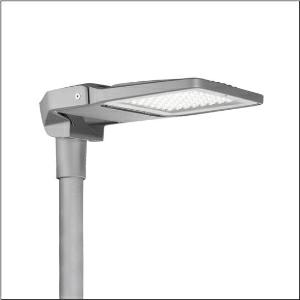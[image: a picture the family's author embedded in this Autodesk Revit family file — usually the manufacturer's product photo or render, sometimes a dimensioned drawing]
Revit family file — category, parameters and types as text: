
# Revit family: floodlight_fl_20_mini___pl61_5xa7672c1c4ac_7b6a
name_source: partatom
category: Lighting Fixtures
units: mm (PartAtom-declared; Revit-internal decimal feet)

## family parameters
Cut with Voids When Loaded = No
Host = Face
Light Source = No
Part Type = Normal
Room Calculation Point = No
Round Connector Dimension = Use Diameter
Shared = No

## types (1)
- --- (1 x LED 3000K / CRI = 80 (unbekannt), 9760 lm, 3000K)
    Apparent Load = 96 VA
    CIE Flux Codes = 33 65 98 100 100
    Color Rendering = 80
    Color Temperature = 3000K
    Default Elevation = 1800 mm
    Description = Floodlight FL 20 mini, floodlight, primary light control with lens, of plastic, primary optical cover: protective disc, of toughened safety glass, transparent, light distribution: PL61, light emission: direct distribution, primary light characteristic: asymmetric, installation type: side-entry, post-top, LED, High Power LED, rated luminous flux: 9.760lm, luminous efficacy: 102lm/W, light colour: 830, colour temperature: 3000K, control gear: ECG Plus, control: flexible luminous flux parameterisation, time-dependent luminous flux control, digital communication interface, overheat protection, power reduction, electronic power reduction, with terminal, 5-pole, max. 2.5mm², mains connection: 220..240V, AC, 50/60Hz, rated input power: 96W, LED unit, of diecast aluminium, powder-coated, Siteco® metallic grey (DB 702S), corrosivity category C5 mid according to DIN EN ISO 12944, incl. 1x M20 cable gland for cable Ø 6.5..12mm, inclination adjustable: 0°, 5°, 10°, 15°, please order mast flange separately, length: 565mm, width: 335mm, height: 119mm, housing frame, of diecast aluminium, powder-coated, Siteco® metallic grey (DB 702S), mast flange adapter, of diecast aluminium, powder-coated, Siteco® metallic grey (DB 702S), DALI, protection rating (complete): IP66, insulation class (complete): insulation class II (safety insulation), certification: CE, ENEC, VDE, protection symbol: D, permissible operating ambient temperature: -40..+40°C, permissible operating ambient temperature for outdoor applications: -40..+50°C, standard: DIN EN 12944, packaging unit: 1 piece

Light Distribution: PL61
    Height = 62 mm  [stored 0.203412 ft]
    Lamp = 1 x LED 3000K / CRI >= 80 (unbekannt)
    Lamp Light Flux = 9760 lm
    Lamp count = 1
    Length = 565 mm
    Luminous efficacy = 102 lm/W
    Manufacturer = Siteco
    ModVariant = No
    Model = 5XA7672C1C4AC
    Number of Poles = 1
    OnlyDefault = Yes
    Power Factor = 1
    Product Name = Floodlight FL 20 mini | PL61
    Product group = floodlight | pylon top
    ProductGroupID = 6101
    Protection Class = Protection class II
    Protection Degree = IP 66
    RLX_Detail_Level = 1
    RLX_Emergency_Light_Flux = 0 lm
    RLX_Emergency_Type = 0
    RLX_Emergency_Type_DB = No
    RlxData = <blob elided: 101853 chars, md5=20a15e5e>
    Socket = socket
    Standby Power = 0 W
    System Light Flux = 9760 lm
    System Power = 96 W
    Type Comments = factory setting: luminous flux: 100 % | dim-lin: 254 | 500 mA
    Type Image = l_1005946.jpg
    URL = http://relux.com
    VarID = @adj_163197
    Voltage = 0 V
    Weight = 0.00 kg
    Width = 335 mm

note: [stored X ft] marks values corroborated as IEEE doubles in the binary element streams (Revit-internal decimal feet)

## geometry (parser evidence)
native form markers: Blend x4, Sweep x11
no freeform markers — native parametric forms only
